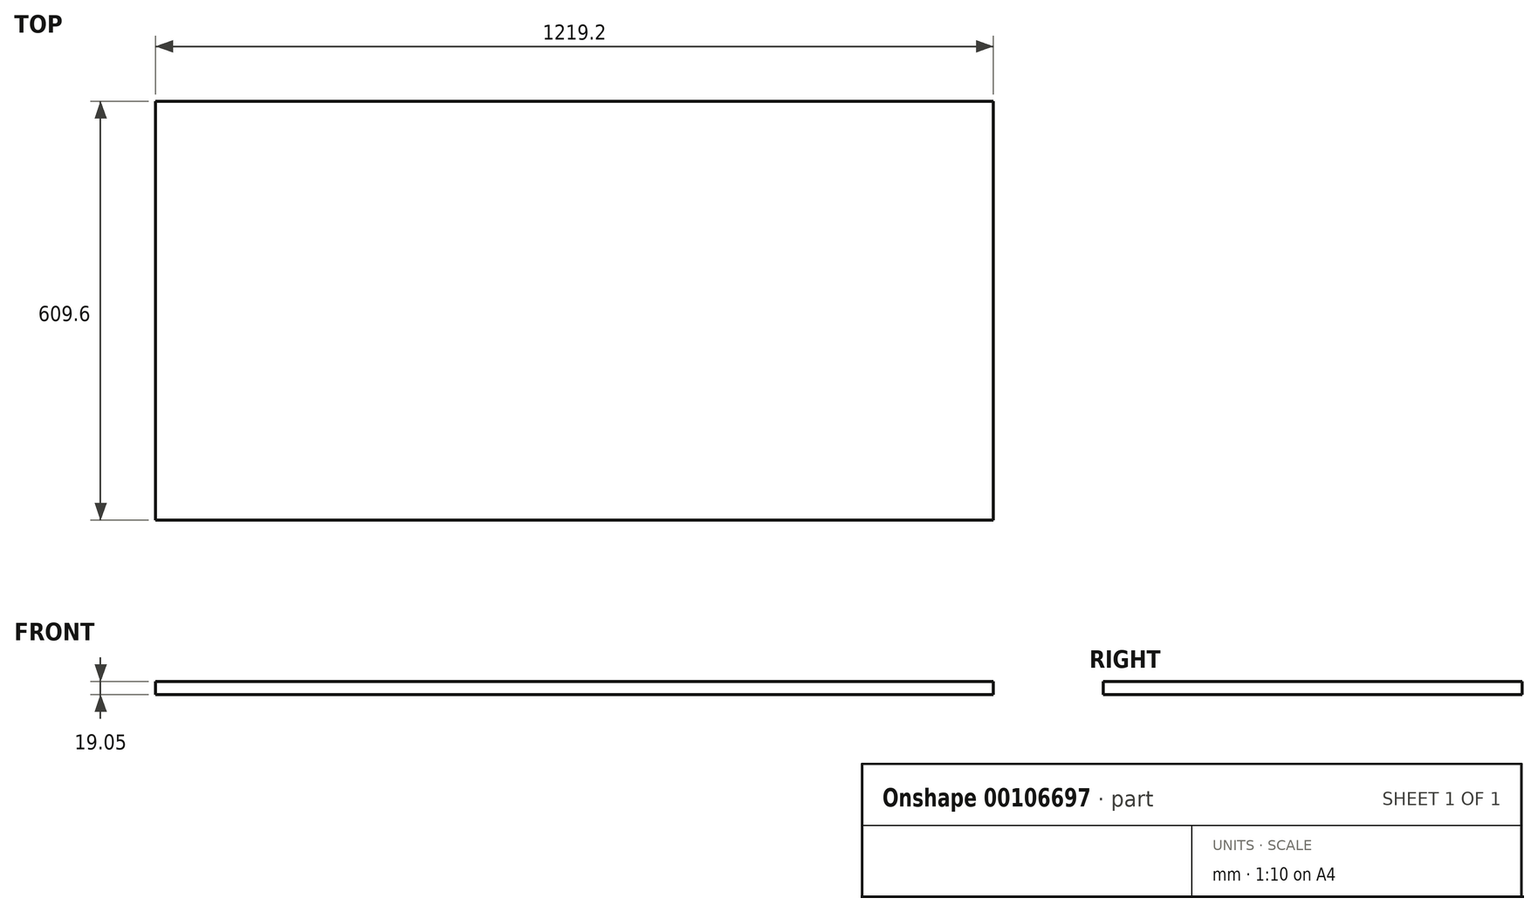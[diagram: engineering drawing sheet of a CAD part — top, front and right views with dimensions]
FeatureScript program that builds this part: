
annotation { "Feature Type Name" : "Feature", "Feature Type Description" : "" }
export const myFeature = defineFeature(function(context is Context, id is Id, definition is map)
    precondition{}
    {
        {
            var Q0;
            Q0=qCreatedBy(makeId("Top.planeOp"),FACE);
            var sketch = newSketch(context, id + "F0", { "sketchPlane" : qUnion([Q0])});
            skLineSegment(sketch, "E0.bottom", {"start": v(0, 0) * mm, "end": v(1219.2, 0) * mm});
            skLineSegment(sketch, "E0.top", {"start": v(0, 609.6) * mm, "end": v(1219.2, 609.6) * mm});
            skLineSegment(sketch, "E0.left", {"start": v(0, 0) * mm, "end": v(0, 609.6) * mm});
            skLineSegment(sketch, "E0.right", {"start": v(1219.2, 0) * mm, "end": v(1219.2, 609.6) * mm});
            skSolve(sketch);
        }
        {
            var Q0;
            Q0=makeQuery(id+"F0.imprint","IMPRINT",FACE,{"disambiguationData":[TD([[makeQuery(id+"F0.imprint","IMPRINT",EDGE,{"derivedFrom":sQuery(id+"F0.wireOp",EDGE,"E0.bottom")}),1.0]])]});
            extrude(context, id + "F1", {"entities" : qUnion([Q0]), "depth" : 19.05 * mm});
        }
    });
